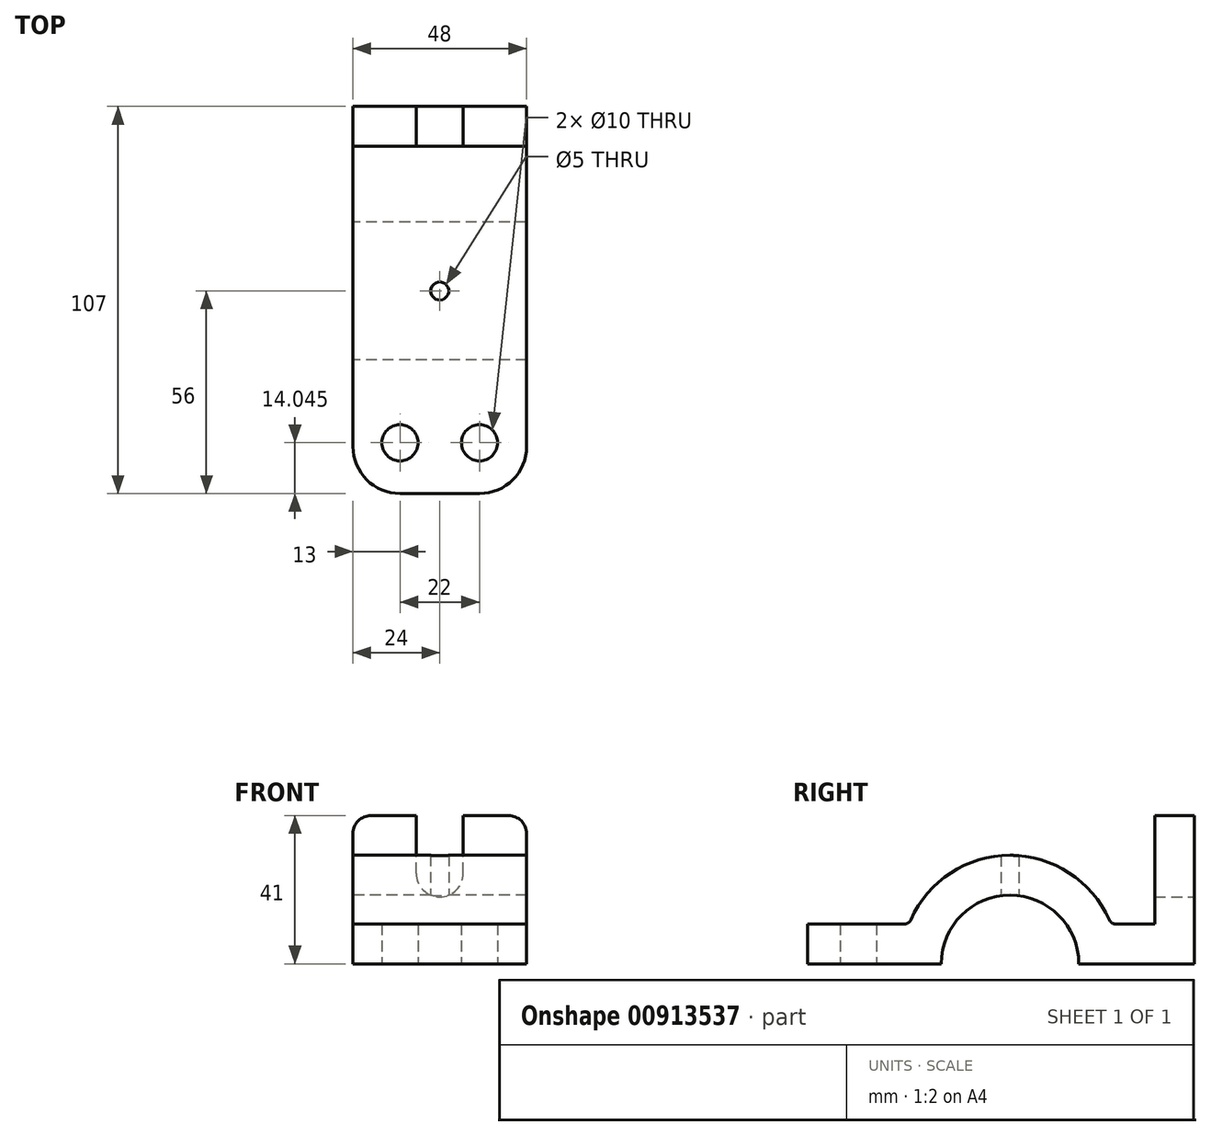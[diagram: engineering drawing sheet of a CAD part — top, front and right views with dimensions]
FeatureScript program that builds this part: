
annotation { "Feature Type Name" : "Feature", "Feature Type Description" : "" }
export const myFeature = defineFeature(function(context is Context, id is Id, definition is map)
    precondition{}
    {
        {
            var Q0;
            Q0=qCreatedBy(makeId("Right.planeOp"),FACE);
            var sketch = newSketch(context, id + "F0", { "sketchPlane" : qUnion([Q0])});
            skCircle(sketch, "E0", {"center": v(0, 0) * mm, "radius": 19 * mm});
            skCircle(sketch, "E1", {"center": v(0, 0) * mm, "radius": 30 * mm});
            skLineSegment(sketch, "E2.bottom", {"start": v(-56, 0) * mm, "end": v(51, 0) * mm});
            skLineSegment(sketch, "E2.top", {"start": v(-56, 11) * mm, "end": v(51, 11) * mm});
            skLineSegment(sketch, "E2.left", {"start": v(-56, 0) * mm, "end": v(-56, 11) * mm});
            skLineSegment(sketch, "E2.right", {"start": v(51, 0) * mm, "end": v(51, 11) * mm});
            skLineSegment(sketch, "E3.bottom", {"start": v(51, 11) * mm, "end": v(40, 11) * mm});
            skLineSegment(sketch, "E3.top", {"start": v(51, 41) * mm, "end": v(40, 41) * mm});
            skLineSegment(sketch, "E3.left", {"start": v(51, 11) * mm, "end": v(51, 41) * mm});
            skLineSegment(sketch, "E3.right", {"start": v(40, 11) * mm, "end": v(40, 41) * mm});
            skSolve(sketch);
        }
        {
            var Q0;
            {var subQ5=sQuery(id+"F0.wireOp",EDGE,"E2.left");Q0=makeQuery(id+"F0.imprint","IMPRINT",FACE,{"disambiguationData":[TD([[makeQuery(id+"F0.imprint","IMPRINT",EDGE,{"derivedFrom":subQ5}),-1.0]])]});}
            var Q1;
            {var subQ0=sQuery(id+"F0.wireOp",EDGE,"E2.bottom");var subQ1=sQuery(id+"F0.wireOp",EDGE,"E0");var subQ2=makeQuery(id+"F0.imprint","INTERSECT",VERTEX,{"disambiguationData":[OD(0.0)],"derivedFrom":[subQ1,subQ0]});Q1=makeQuery(id+"F0.imprint","IMPRINT",FACE,{"disambiguationData":[TD([[makeQuery(id+"F0.imprint","IMPRINT",EDGE,{"disambiguationData":[TD([[subQ2,1.0]])],"derivedFrom":subQ1}),-1.0]])]});}
            var Q2;
            {var subQ0=sQuery(id+"F0.wireOp",EDGE,"E2.top");var subQ1=sQuery(id+"F0.wireOp",EDGE,"E0");var subQ2=makeQuery(id+"F0.imprint","INTERSECT",VERTEX,{"disambiguationData":[OD(0.0)],"derivedFrom":[subQ1,subQ0]});Q2=makeQuery(id+"F0.imprint","IMPRINT",FACE,{"disambiguationData":[TD([[makeQuery(id+"F0.imprint","IMPRINT",EDGE,{"disambiguationData":[TD([[subQ2,1.0]])],"derivedFrom":subQ1}),-1.0]])]});}
            var Q3;
            {var subQ0=sQuery(id+"F0.wireOp",EDGE,"E2.top");var subQ1=sQuery(id+"F0.wireOp",EDGE,"E0");var subQ2=makeQuery(id+"F0.imprint","INTERSECT",VERTEX,{"disambiguationData":[OD(1.0)],"derivedFrom":[subQ1,subQ0]});Q3=makeQuery(id+"F0.imprint","IMPRINT",FACE,{"disambiguationData":[TD([[makeQuery(id+"F0.imprint","IMPRINT",EDGE,{"disambiguationData":[TD([[subQ2,1.0]])],"derivedFrom":subQ1}),-1.0]])]});}
            var Q4;
            {var subQ0=sQuery(id+"F0.wireOp",EDGE,"E2.right");Q4=makeQuery(id+"F0.imprint","IMPRINT",FACE,{"disambiguationData":[TD([[makeQuery(id+"F0.imprint","IMPRINT",EDGE,{"derivedFrom":subQ0}),1.0]])]});}
            var Q5;
            Q5=makeQuery(id+"F0.imprint","IMPRINT",FACE,{"disambiguationData":[TD([[makeQuery(id+"F0.imprint","IMPRINT",EDGE,{"derivedFrom":sQuery(id+"F0.wireOp",EDGE,"E3.top")}),1.0]])]});
            extrude(context, id + "F1", {"entities" : qUnion([Q0, Q1, Q2, Q3, Q4, Q5]), "endBound" : BoundingType.SYMMETRIC, "depth" : 48 * mm, "offsetDistance" : 25 * mm});
        }
        {
            var Q0;
            Q0=makeQuery(id+"F1.opExtrude","SWEPT_FACE",FACE,{"disambiguationData":[OSD([sQuery(id+"F0.wireOp",EDGE,"E2.right"),sQuery(id+"F0.wireOp",EDGE,"E3.left")])]});
            var sketch = newSketch(context, id + "F2", { "sketchPlane" : qUnion([Q0])});
            skLineSegment(sketch, "E4", {"start": v(0, 0) * mm, "end": v(0, 41) * mm, "construction": true});
            skCircle(sketch, "E5", {"center": v(0, 25) * mm, "radius": 6.5 * mm});
            skLineSegment(sketch, "E6", {"start": v(-6.5, 25) * mm, "end": v(-6.5, 41) * mm});
            skLineSegment(sketch, "E7", {"start": v(6.5, 25) * mm, "end": v(6.5, 41) * mm});
            skSolve(sketch);
        }
        {
            var Q0;
            {var subQ0=sQuery(id+"F2.wireOp",EDGE,"E5");var subQ2=makeQuery(id+"F2.imprint","INTERSECT",VERTEX,{"derivedFrom":[subQ0,sQuery(id+"F2.wireOp",EDGE,"E6")]});Q0=makeQuery(id+"F2.imprint","IMPRINT",FACE,{"disambiguationData":[TD([[makeQuery(id+"F2.imprint","IMPRINT",EDGE,{"disambiguationData":[TD([[subQ2,1.0]])],"derivedFrom":subQ0}),1.0]])]});}
            var Q1;
            {var subQ2=sQuery(id+"F2.wireOp",EDGE,"E6");Q1=makeQuery(id+"F2.imprint","IMPRINT",FACE,{"disambiguationData":[TD([[makeQuery(id+"F2.imprint","IMPRINT",EDGE,{"derivedFrom":subQ2}),-1.0]])]});}
            var Q2;
            Q2 = qSketchRegion(id + "F4", true);
            var Q3;
            Q3=makeQuery(id+"F1.opExtrude","SWEPT_FACE",FACE,{"disambiguationData":[OSD([sQuery(id+"F0.wireOp",EDGE,"E3.right")])]});
            extrude(context, id + "F3", {"entities" : qUnion([Q0, Q1, Q2]), "operationType" : NewBodyOperationType.REMOVE, "endBound" : BoundingType.UP_TO_SURFACE, "oppositeDirection" : true, "endBoundEntityFace" : qUnion([Q3]), "offsetDistance" : 25 * mm, "depth" : 25 * mm});
        }
        {
            var Q0;
            Q0=qCreatedBy(makeId("Top.planeOp"),FACE);
            var sketch = newSketch(context, id + "F4", { "sketchPlane" : qUnion([Q0])});
            skCircle(sketch, "E8", {"center": v(0, 0) * mm, "radius": 2.5 * mm});
            skLineSegment(sketch, "E9", {"start": v(24, -41.96) * mm, "end": v(-24, -41.96) * mm, "construction": true});
            skLineSegment(sketch, "E10", {"start": v(0, -56) * mm, "end": v(0, -27.91) * mm, "construction": true});
            skCircle(sketch, "E11", {"center": v(-11, -41.96) * mm, "radius": 5 * mm});
            skCircle(sketch, "E12", {"center": v(11, -41.96) * mm, "radius": 5 * mm});
            skSolve(sketch);
        }
        {
            var Q0;
            Q0=qSketchRegion(id+"F4",true);
            extrude(context, id + "F5", {"entities" : qUnion([Q0]), "operationType" : NewBodyOperationType.REMOVE, "endBound" : BoundingType.THROUGH_ALL, "depth" : 25 * mm, "offsetDistance" : 25 * mm});
        }
        {
            var Q0;
            Q0=makeQuery(id+"F1.opExtrude","CAP_EDGE",EDGE,{"disambiguationData":[OSD([sQuery(id+"F0.wireOp",EDGE,"E2.left")])],"isStart":false});
            var Q1;
            Q1=makeQuery(id+"F1.opExtrude","CAP_EDGE",EDGE,{"disambiguationData":[OSD([sQuery(id+"F0.wireOp",EDGE,"E2.left")])],"isStart":true});
            fillet(context, id + "F6", {"entities" : qUnion([Q0, Q1]), "radius" : 13 * mm, "tangentPropagation" : true, "allowEdgeOverflow" : false});
        }
        {
            var Q0;
            Q0=makeQuery(id+"F1.opExtrude","CAP_EDGE",EDGE,{"disambiguationData":[OSD([sQuery(id+"F0.wireOp",EDGE,"E3.top")])],"isStart":false});
            var Q1;
            Q1=makeQuery(id+"F1.opExtrude","CAP_EDGE",EDGE,{"disambiguationData":[OSD([sQuery(id+"F0.wireOp",EDGE,"E3.top")])],"isStart":true});
            fillet(context, id + "F7", {"entities" : qUnion([Q0, Q1]), "radius" : 5 * mm, "tangentPropagation" : true, "allowEdgeOverflow" : false});
        }
        {
            var Q0;
            {var subQ0=sQuery(id+"F0.wireOp",EDGE,"E2.top");var subQ1=sQuery(id+"F0.wireOp",EDGE,"E1");Q0=makeQuery(id+"F1.opExtrude","SWEPT_EDGE",EDGE,{"disambiguationData":[OSD([subQ1,subQ0]),TDD([makeQuery(id+"F0.imprint","INTERSECT",VERTEX,{"disambiguationData":[OD(1.0)],"derivedFrom":[subQ1,subQ0]})])]});}
            var Q1;
            {var subQ0=sQuery(id+"F0.wireOp",EDGE,"E2.top");var subQ1=sQuery(id+"F0.wireOp",EDGE,"E1");Q1=makeQuery(id+"F1.opExtrude","SWEPT_EDGE",EDGE,{"disambiguationData":[OSD([subQ1,subQ0]),TDD([makeQuery(id+"F0.imprint","INTERSECT",VERTEX,{"disambiguationData":[OD(0.0)],"derivedFrom":[subQ1,subQ0]})])]});}
            fillet(context, id + "F8", {"entities" : qUnion([Q0, Q1]), "radius" : 2 * mm, "tangentPropagation" : true, "allowEdgeOverflow" : false});
        }
    });
